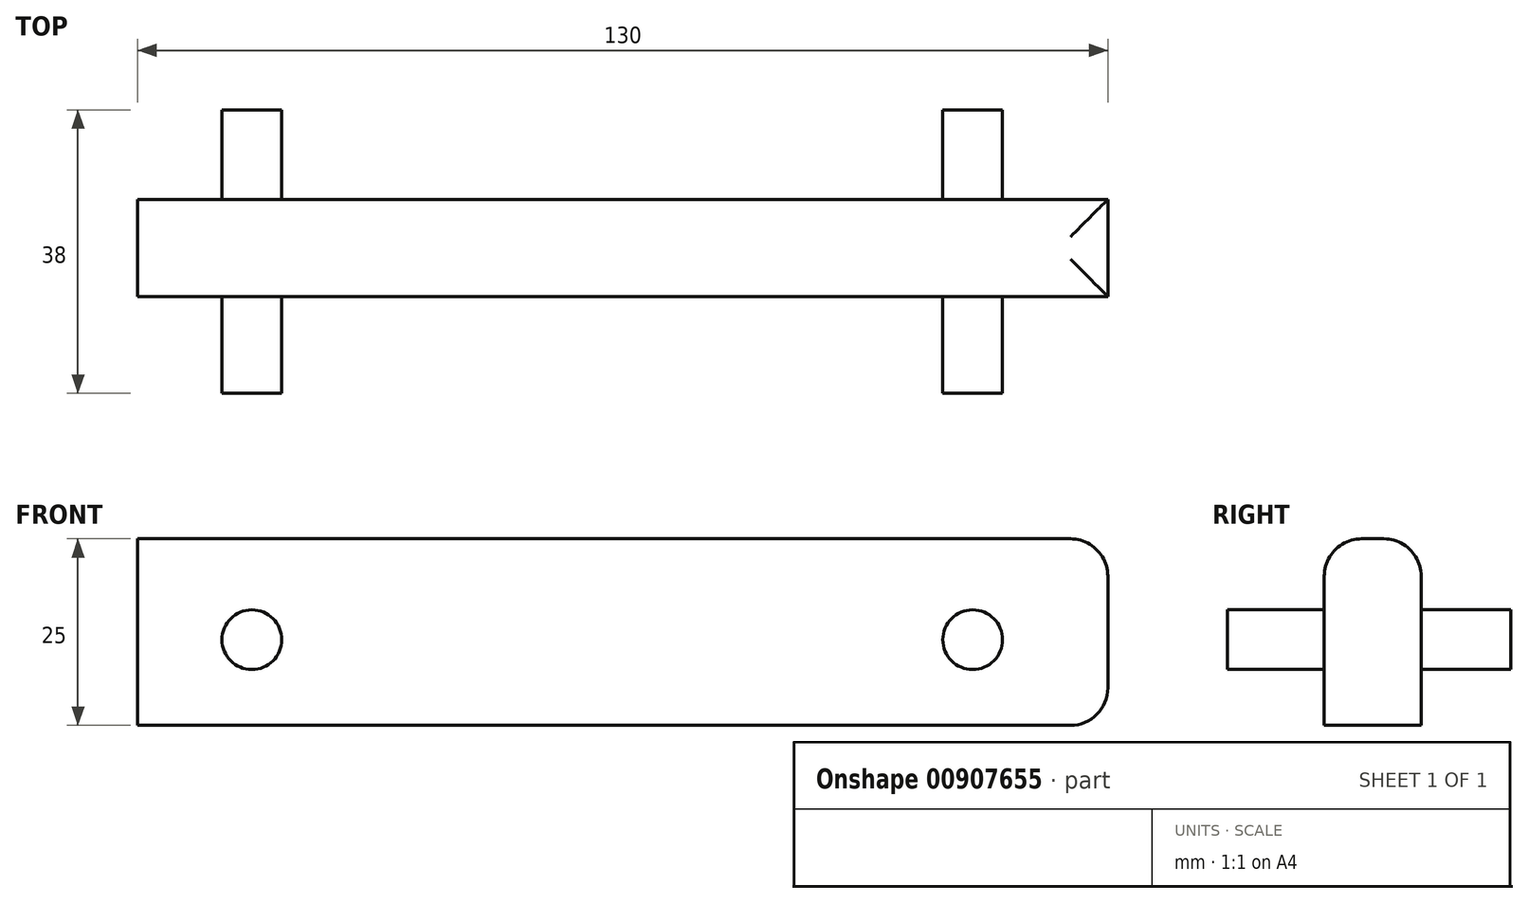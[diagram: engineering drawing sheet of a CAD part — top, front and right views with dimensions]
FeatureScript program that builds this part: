
annotation { "Feature Type Name" : "Feature", "Feature Type Description" : "" }
export const myFeature = defineFeature(function(context is Context, id is Id, definition is map)
    precondition{}
    {
        {
            var Q0;
            Q0=qCreatedBy(makeId("Top.planeOp"),FACE);
            var sketch = newSketch(context, id + "F0", { "sketchPlane" : qUnion([Q0])});
            skLineSegment(sketch, "E0.bottom", {"start": v(5729.17, -32.15) * mm, "end": v(-35.83, -32.15) * mm});
            skLineSegment(sketch, "E0.top", {"start": v(5729.17, 14.3) * mm, "end": v(-35.83, 14.3) * mm});
            skLineSegment(sketch, "E0.left", {"start": v(5729.17, -32.15) * mm, "end": v(5729.17, 14.3) * mm});
            skLineSegment(sketch, "E0.right", {"start": v(-35.83, -32.15) * mm, "end": v(-35.83, 14.3) * mm});
            skLineSegment(sketch, "E1.bottom", {"start": v(57.9, -45.21) * mm, "end": v(-72.1, -45.21) * mm});
            skLineSegment(sketch, "E1.top", {"start": v(57.9, -58.21) * mm, "end": v(-72.1, -58.21) * mm});
            skLineSegment(sketch, "E1.left", {"start": v(57.9, -45.21) * mm, "end": v(57.9, -58.21) * mm});
            skLineSegment(sketch, "E1.right", {"start": v(-72.1, -45.21) * mm, "end": v(-72.1, -58.21) * mm});
            skSolve(sketch);
        }
        {
            var Q0;
            Q0=makeQuery(id+"F0.imprint","IMPRINT",FACE,{"disambiguationData":[TD([[makeQuery(id+"F0.imprint","IMPRINT",EDGE,{"derivedFrom":sQuery(id+"F0.wireOp",EDGE,"E1.bottom")}),1.0]])]});
            extrude(context, id + "F1", {"entities" : qUnion([Q0]), "depth" : 25 * mm, "offsetDistance" : 25 * mm});
        }
        {
            var Q0;
            Q0=makeQuery(id+"F1.opExtrude","SWEPT_FACE",FACE,{"disambiguationData":[OSD([sQuery(id+"F0.wireOp",EDGE,"E1.bottom")])]});
            var sketch = newSketch(context, id + "F2", { "sketchPlane" : qUnion([Q0])});
            skCircle(sketch, "E2", {"center": v(-39.8, 11.47) * mm, "radius": 4 * mm});
            skCircle(sketch, "E3", {"center": v(56.8, 11.47) * mm, "radius": 4 * mm});
            skSolve(sketch);
        }
        {
            var Q0;
            Q0=makeQuery(id+"F2.imprint","IMPRINT",FACE,{"disambiguationData":[TD([[makeQuery(id+"F2.imprint","IMPRINT",EDGE,{"derivedFrom":sQuery(id+"F2.wireOp",EDGE,"E2")}),1.0]])]});
            var Q1;
            Q1=makeQuery(id+"F2.imprint","IMPRINT",FACE,{"disambiguationData":[TD([[makeQuery(id+"F2.imprint","IMPRINT",EDGE,{"derivedFrom":sQuery(id+"F2.wireOp",EDGE,"E3")}),1.0]])]});
            extrude(context, id + "F3", {"entities" : qUnion([Q0, Q1]), "operationType" : NewBodyOperationType.ADD, "depth" : 25 * mm, "offsetDistance" : 25 * mm});
        }
        {
            var Q0;
            Q0=makeQuery(id+"F3.opExtrude","CAP_FACE",FACE,{"disambiguationData":[OSD([sQuery(id+"F2.wireOp",EDGE,"E2")])],"isStart":false});
            var Q1;
            Q1=makeQuery(id+"F3.opExtrude","CAP_FACE",FACE,{"disambiguationData":[OSD([sQuery(id+"F2.wireOp",EDGE,"E3")])],"isStart":false});
            extrude(context, id + "F4", {"entities" : qUnion([Q0, Q1]), "operationType" : NewBodyOperationType.REMOVE, "oppositeDirection" : true, "depth" : 99.4 * mm, "offsetDistance" : 25 * mm});
        }
        {
            var Q0;
            Q0=makeQuery(id+"F1.opExtrude","CAP_EDGE",EDGE,{"disambiguationData":[OSD([sQuery(id+"F0.wireOp",EDGE,"E1.left")])],"isStart":false});
            var Q1;
            Q1=makeQuery(id+"F1.opExtrude","CAP_EDGE",EDGE,{"disambiguationData":[OSD([sQuery(id+"F0.wireOp",EDGE,"E1.left")])],"isStart":true});
            var Q2;
            Q2=makeQuery(id+"F1.opExtrude","CAP_EDGE",EDGE,{"disambiguationData":[OSD([sQuery(id+"F0.wireOp",EDGE,"E1.top")])],"isStart":false});
            var Q3;
            Q3=makeQuery(id+"F1.opExtrude","CAP_EDGE",EDGE,{"disambiguationData":[OSD([sQuery(id+"F0.wireOp",EDGE,"E1.bottom")])],"isStart":false});
            fillet(context, id + "F5", {"entities" : qUnion([Q0, Q1, Q2, Q3]), "radius" : 5 * mm, "tangentPropagation" : true, "allowEdgeOverflow" : false});
        }
        {
            var Q0;
            Q0=makeQuery(id+"F1.opExtrude","SWEPT_FACE",FACE,{"disambiguationData":[OSD([sQuery(id+"F0.wireOp",EDGE,"E1.top")])]});
            var sketch = newSketch(context, id + "F6", { "sketchPlane" : qUnion([Q0])});
            skCircle(sketch, "E4.0", {"center": v(-56.8, 11.47) * mm, "radius": 4 * mm});
            skCircle(sketch, "E5.0", {"center": v(39.8, 11.47) * mm, "radius": 4 * mm});
            skSolve(sketch);
        }
        {
            var Q0;
            Q0=makeQuery(id+"F6.imprint","IMPRINT",FACE,{"disambiguationData":[TD([[makeQuery(id+"F6.imprint","IMPRINT",EDGE,{"derivedFrom":sQuery(id+"F6.wireOp",EDGE,"E4.0")}),1.0]])]});
            var Q1;
            Q1=makeQuery(id+"F6.imprint","IMPRINT",FACE,{"disambiguationData":[TD([[makeQuery(id+"F6.imprint","IMPRINT",EDGE,{"derivedFrom":sQuery(id+"F6.wireOp",EDGE,"E5.0")}),1.0]])]});
            extrude(context, id + "F7", {"entities" : qUnion([Q0, Q1]), "operationType" : NewBodyOperationType.ADD, "depth" : 13 * mm, "offsetDistance" : 25 * mm, "hasSecondDirection" : true, "secondDirectionOppositeDirection" : true, "secondDirectionDepth" : 25 * mm});
        }
    });
